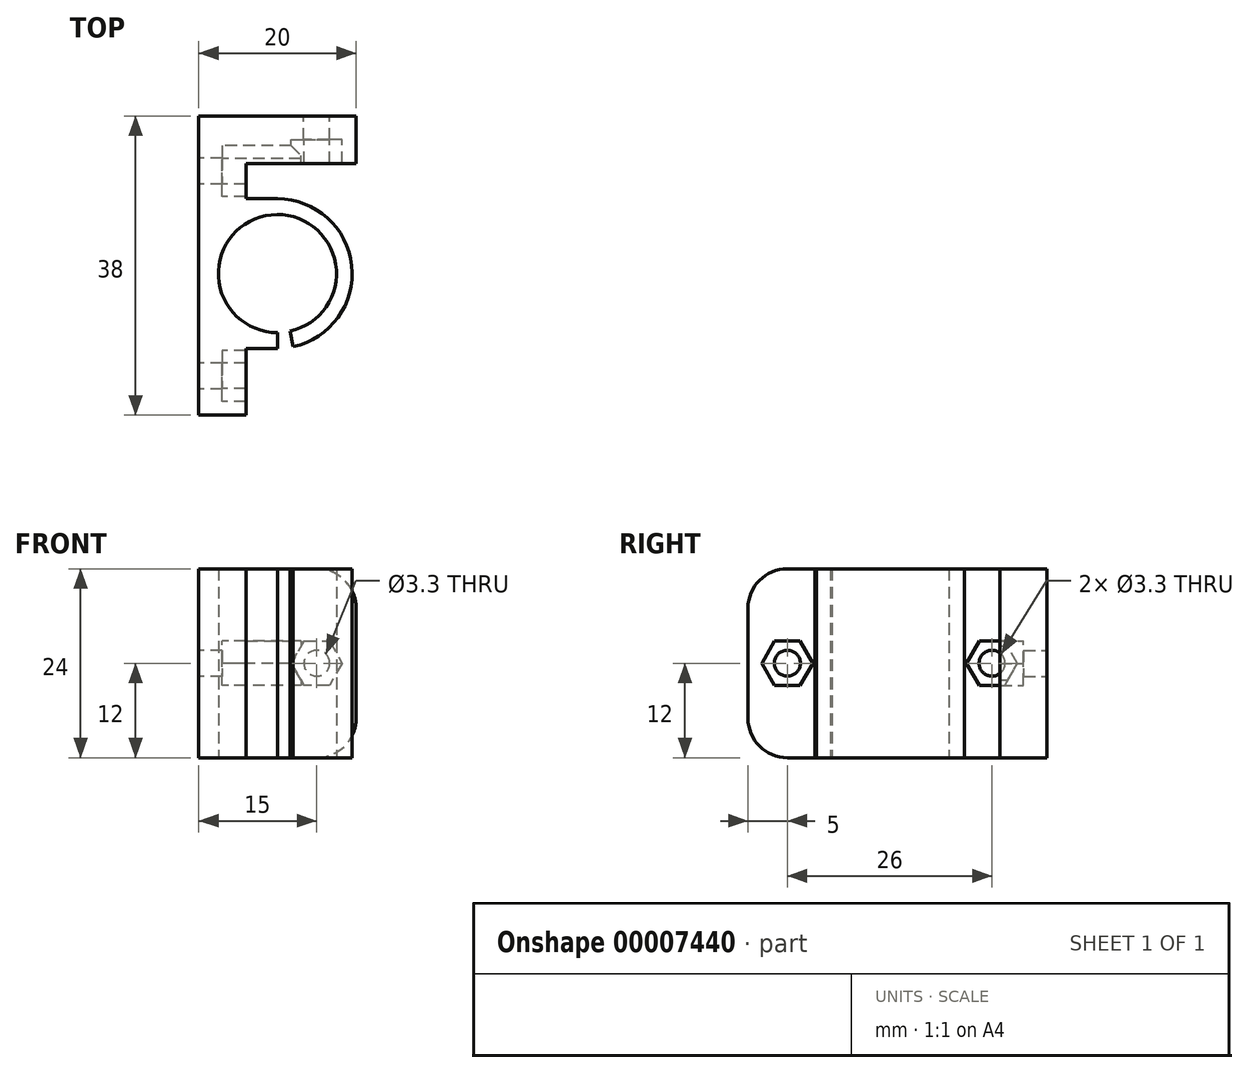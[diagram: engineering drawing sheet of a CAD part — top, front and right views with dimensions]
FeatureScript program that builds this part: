
annotation { "Feature Type Name" : "Feature", "Feature Type Description" : "" }
export const myFeature = defineFeature(function(context is Context, id is Id, definition is map)
    precondition{}
    {
        {
            var Q0;
            Q0=qCreatedBy(makeId("Top.planeOp"),FACE);
            var sketch = newSketch(context, id + "F0", { "sketchPlane" : qUnion([Q0])});
            skLineSegment(sketch, "E0", {"start": v(0, 0) * mm, "end": v(20, 0) * mm});
            skLineSegment(sketch, "E1", {"start": v(0, 0) * mm, "end": v(0, -38) * mm});
            skLineSegment(sketch, "E2", {"start": v(0, -38) * mm, "end": v(6, -38) * mm});
            skCircle(sketch, "E3", {"center": v(10, -20) * mm, "radius": 9.5 * mm});
            skCircle(sketch, "E4", {"center": v(10, -20) * mm, "radius": 7.5 * mm});
            skLineSegment(sketch, "E5", {"start": v(6, -38) * mm, "end": v(6, -28.62) * mm});
            skLineSegment(sketch, "E6", {"start": v(20, 0) * mm, "end": v(20, -6) * mm});
            skLineSegment(sketch, "E7", {"start": v(20, -6) * mm, "end": v(6, -6) * mm});
            skLineSegment(sketch, "E8", {"start": v(6, -6) * mm, "end": v(6, -11.38) * mm});
            skLineSegment(sketch, "E9", {"start": v(6, -11.38) * mm, "end": v(6, -28.62) * mm, "construction": true});
            skLineSegment(sketch, "E10", {"start": v(10, -10.5) * mm, "end": v(6, -10.5) * mm});
            skLineSegment(sketch, "E11", {"start": v(10, -29.5) * mm, "end": v(6, -29.5) * mm});
            skLineSegment(sketch, "E12", {"start": v(10, -29.5) * mm, "end": v(10, -27.5) * mm});
            skLineSegment(sketch, "E13", {"start": v(10, -27.5) * mm, "end": v(10, -20) * mm});
            skLineSegment(sketch, "E14", {"start": v(12, -29.29) * mm, "end": v(10, -20) * mm});
            skPoint(sketch, "E15", {"position": v(11.58, -27.33) * mm});
            skSolve(sketch);
        }
        {
            var Q0;
            Q0=makeQuery(id+"F0.imprint","IMPRINT",FACE,{"disambiguationData":[TD([[makeQuery(id+"F0.imprint","IMPRINT",EDGE,{"derivedFrom":sQuery(id+"F0.wireOp",EDGE,"E0")}),-1.0]])]});
            var Q1;
            {var subQ5=sQuery(id+"F0.wireOp",EDGE,"E12");Q1=makeQuery(id+"F0.imprint","IMPRINT",FACE,{"disambiguationData":[TD([[makeQuery(id+"F0.imprint","IMPRINT",EDGE,{"derivedFrom":subQ5}),1.0]])]});}
            var Q2;
            {var subQ0=sQuery(id+"F0.wireOp",EDGE,"E11");Q2=makeQuery(id+"F0.imprint","IMPRINT",FACE,{"disambiguationData":[TD([[makeQuery(id+"F0.imprint","IMPRINT",EDGE,{"derivedFrom":subQ0}),-1.0]])]});}
            var Q3;
            {var subQ0=sQuery(id+"F0.wireOp",EDGE,"E10");Q3=makeQuery(id+"F0.imprint","IMPRINT",FACE,{"disambiguationData":[TD([[makeQuery(id+"F0.imprint","IMPRINT",EDGE,{"derivedFrom":subQ0}),1.0]])]});}
            extrude(context, id + "F1", {"entities" : qUnion([Q0, Q1, Q2, Q3]), "depth" : 24 * mm});
        }
        {
            var Q0;
            Q0=makeQuery(id+"F1.opExtrude","SWEPT_FACE",FACE,{"disambiguationData":[OSD([sQuery(id+"F0.wireOp",EDGE,"E1")])]});
            cPlane(context, id + "F2", {"entities" : qUnion([Q0]), "cplaneType" : CPlaneType.OFFSET, "offset" : 3 * mm, "oppositeDirection" : true, "width" : 150 * mm, "height" : 150 * mm});
        }
        {
            var Q0;
            Q0=qCreatedBy(id+"F2.planeOp",FACE);
            var sketch = newSketch(context, id + "F3", { "sketchPlane" : qUnion([Q0])});
            skLineSegment(sketch, "E16", {"start": v(7, 12) * mm, "end": v(20, 12) * mm, "construction": true});
            skLineSegment(sketch, "E17", {"start": v(20, 12) * mm, "end": v(33, 12) * mm, "construction": true});
            skCircle(sketch, "E18", {"center": v(7, 12) * mm, "radius": 1.65 * mm});
            skCircle(sketch, "E19", {"center": v(33, 12) * mm, "radius": 1.65 * mm});
            skCircle(sketch, "E20.cCircle", {"center": v(7, 12) * mm, "radius": 2.8 * mm, "construction": true});
            skLineSegment(sketch, "E20.0", {"start": v(5.38, 14.8) * mm, "end": v(8.62, 14.8) * mm});
            skLineSegment(sketch, "E20.1", {"start": v(8.62, 14.8) * mm, "end": v(10.23, 12) * mm});
            skLineSegment(sketch, "E20.2", {"start": v(10.23, 12) * mm, "end": v(8.62, 9.2) * mm});
            skLineSegment(sketch, "E20.3", {"start": v(8.62, 9.2) * mm, "end": v(5.38, 9.2) * mm});
            skLineSegment(sketch, "E20.4", {"start": v(5.38, 9.2) * mm, "end": v(3.77, 12) * mm});
            skLineSegment(sketch, "E20.5", {"start": v(3.77, 12) * mm, "end": v(5.38, 14.8) * mm});
            skPoint(sketch, "E20.0.midPoint", {"position": v(7, 14.8) * mm});
            skCircle(sketch, "E21.cCircle", {"center": v(33, 12) * mm, "radius": 2.8 * mm, "construction": true});
            skLineSegment(sketch, "E21.0", {"start": v(31.38, 14.8) * mm, "end": v(34.62, 14.8) * mm});
            skLineSegment(sketch, "E21.1", {"start": v(34.62, 14.8) * mm, "end": v(36.23, 12) * mm});
            skLineSegment(sketch, "E21.2", {"start": v(36.23, 12) * mm, "end": v(34.62, 9.2) * mm});
            skLineSegment(sketch, "E21.3", {"start": v(34.62, 9.2) * mm, "end": v(31.38, 9.2) * mm});
            skLineSegment(sketch, "E21.4", {"start": v(31.38, 9.2) * mm, "end": v(29.77, 12) * mm});
            skLineSegment(sketch, "E21.5", {"start": v(29.77, 12) * mm, "end": v(31.38, 14.8) * mm});
            skPoint(sketch, "E21.0.midPoint", {"position": v(33, 14.8) * mm});
            skSolve(sketch);
        }
        {
            var Q0;
            Q0=makeQuery(id+"F3.imprint","IMPRINT",FACE,{"disambiguationData":[TD([[makeQuery(id+"F3.imprint","IMPRINT",EDGE,{"derivedFrom":sQuery(id+"F3.wireOp",EDGE,"E18")}),1.0]])]});
            var Q1;
            Q1=makeQuery(id+"F3.imprint","IMPRINT",FACE,{"disambiguationData":[TD([[makeQuery(id+"F3.imprint","IMPRINT",EDGE,{"derivedFrom":sQuery(id+"F3.wireOp",EDGE,"E19")}),1.0]])]});
            extrude(context, id + "F4", {"entities" : qUnion([Q0, Q1]), "operationType" : NewBodyOperationType.REMOVE, "oppositeDirection" : true, "depth" : 10 * mm, "hasSecondDirection" : true, "secondDirectionBound" : BoundingType.THROUGH_ALL, "secondDirectionOppositeDirection" : false, "secondDirectionDepth" : 25 * mm});
        }
        {
            var Q0;
            Q0 = qSketchRegion(id + "F3", true);
            extrude(context, id + "F5", {"entities" : qUnion([Q0]), "operationType" : NewBodyOperationType.REMOVE, "oppositeDirection" : true, "depth" : 10 * mm});
        }
        {
            var Q0;
            Q0=makeQuery(id+"F1.opExtrude","SWEPT_FACE",FACE,{"disambiguationData":[OSD([sQuery(id+"F0.wireOp",EDGE,"E0")])]});
            cPlane(context, id + "F6", {"entities" : qUnion([Q0]), "cplaneType" : CPlaneType.OFFSET, "offset" : 3 * mm, "oppositeDirection" : true, "width" : 150 * mm, "height" : 150 * mm});
        }
        {
            var Q0;
            Q0=qCreatedBy(id+"F6.planeOp",FACE);
            var sketch = newSketch(context, id + "F7", { "sketchPlane" : qUnion([Q0])});
            skCircle(sketch, "E22", {"center": v(-15, 12) * mm, "radius": 1.65 * mm});
            skCircle(sketch, "E23.cCircle", {"center": v(-15, 12) * mm, "radius": 2.8 * mm, "construction": true});
            skLineSegment(sketch, "E23.0", {"start": v(-16.62, 14.8) * mm, "end": v(-13.38, 14.8) * mm});
            skLineSegment(sketch, "E23.1", {"start": v(-13.38, 14.8) * mm, "end": v(-11.77, 12) * mm});
            skLineSegment(sketch, "E23.2", {"start": v(-11.77, 12) * mm, "end": v(-13.38, 9.2) * mm});
            skLineSegment(sketch, "E23.3", {"start": v(-13.38, 9.2) * mm, "end": v(-16.62, 9.2) * mm});
            skLineSegment(sketch, "E23.4", {"start": v(-16.62, 9.2) * mm, "end": v(-18.23, 12) * mm});
            skLineSegment(sketch, "E23.5", {"start": v(-18.23, 12) * mm, "end": v(-16.62, 14.8) * mm});
            skPoint(sketch, "E23.0.midPoint", {"position": v(-15, 14.8) * mm});
            skSolve(sketch);
        }
        {
            var Q0;
            Q0 = qSketchRegion(id + "F7", true);
            extrude(context, id + "F8", {"entities" : qUnion([Q0]), "operationType" : NewBodyOperationType.REMOVE, "oppositeDirection" : true, "depth" : 6 * mm});
        }
        {
            var Q0;
            Q0=makeQuery(id+"F7.imprint","IMPRINT",FACE,{"disambiguationData":[TD([[makeQuery(id+"F7.imprint","IMPRINT",EDGE,{"derivedFrom":sQuery(id+"F7.wireOp",EDGE,"E22")}),1.0]])]});
            extrude(context, id + "F9", {"entities" : qUnion([Q0]), "operationType" : NewBodyOperationType.REMOVE, "oppositeDirection" : true, "depth" : 7 * mm, "hasSecondDirection" : true, "secondDirectionBound" : BoundingType.THROUGH_ALL, "secondDirectionOppositeDirection" : false, "secondDirectionDepth" : 25 * mm});
        }
        {
            var Q0;
            Q0=makeQuery(id+"F1.opExtrude","CAP_EDGE",EDGE,{"disambiguationData":[OSD([sQuery(id+"F0.wireOp",EDGE,"E2")])],"isStart":false});
            var Q1;
            Q1=makeQuery(id+"F1.opExtrude","CAP_EDGE",EDGE,{"disambiguationData":[OSD([sQuery(id+"F0.wireOp",EDGE,"E6")])],"isStart":false});
            var Q2;
            Q2=makeQuery(id+"F1.opExtrude","CAP_EDGE",EDGE,{"disambiguationData":[OSD([sQuery(id+"F0.wireOp",EDGE,"E6")])],"isStart":true});
            var Q3;
            Q3=makeQuery(id+"F1.opExtrude","CAP_EDGE",EDGE,{"disambiguationData":[OSD([sQuery(id+"F0.wireOp",EDGE,"E2")])],"isStart":true});
            fillet(context, id + "F10", {"entities" : qUnion([Q0, Q1, Q2, Q3]), "radius" : 5 * mm, "tangentPropagation" : true, "allowEdgeOverflow" : false});
        }
    });
